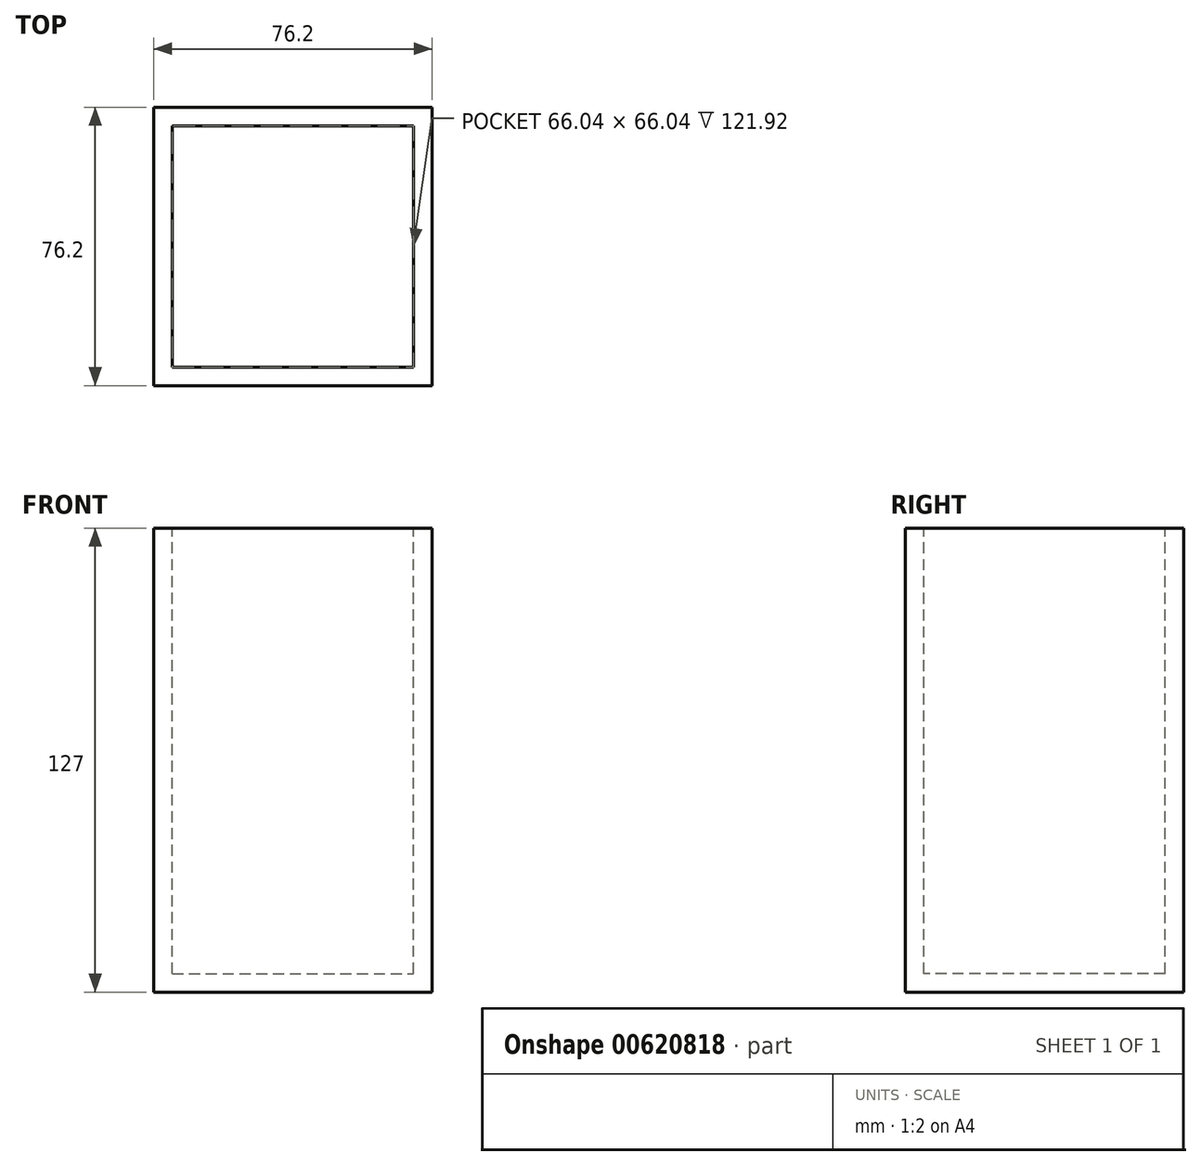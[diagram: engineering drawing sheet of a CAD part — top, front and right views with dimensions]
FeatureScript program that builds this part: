
annotation { "Feature Type Name" : "Feature", "Feature Type Description" : "" }
export const myFeature = defineFeature(function(context is Context, id is Id, definition is map)
    precondition{}
    {
        {
            var Q0;
            Q0=qCreatedBy(makeId("Top.planeOp"),FACE);
            var sketch = newSketch(context, id + "F0", { "sketchPlane" : qUnion([Q0])});
            skLineSegment(sketch, "E0.bottom", {"start": v(-38.1, 38.1) * mm, "end": v(38.1, 38.1) * mm});
            skLineSegment(sketch, "E0.top", {"start": v(-38.1, -38.1) * mm, "end": v(38.1, -38.1) * mm});
            skLineSegment(sketch, "E0.left", {"start": v(-38.1, 38.1) * mm, "end": v(-38.1, -38.1) * mm});
            skLineSegment(sketch, "E0.right", {"start": v(38.1, 38.1) * mm, "end": v(38.1, -38.1) * mm});
            skPoint(sketch, "E0.middle", {"position": v(0, 0) * mm});
            skSolve(sketch);
        }
        {
            var Q0;
            Q0=makeQuery(id+"F0.imprint","IMPRINT",FACE,{"disambiguationData":[TD([[makeQuery(id+"F0.imprint","IMPRINT",EDGE,{"derivedFrom":sQuery(id+"F0.wireOp",EDGE,"E0.bottom")}),-1.0]])]});
            extrude(context, id + "F1", {"entities" : qUnion([Q0]), "oppositeDirection" : true, "depth" : 127 * mm, "offsetDistance" : 25.4 * mm});
        }
        {
            var Q0;
            Q0=makeQuery(id+"F1.opExtrude","CAP_FACE",FACE,{"disambiguationData":[OSD([sQuery(id+"F0.wireOp",EDGE,"E0.bottom"),sQuery(id+"F0.wireOp",EDGE,"E0.top"),sQuery(id+"F0.wireOp",EDGE,"E0.left"),sQuery(id+"F0.wireOp",EDGE,"E0.right")])],"isStart":true});
            shell(context, id + "F2", {"entities" : qUnion([Q0]), "thickness" : 5.08 * mm});
        }
    });
